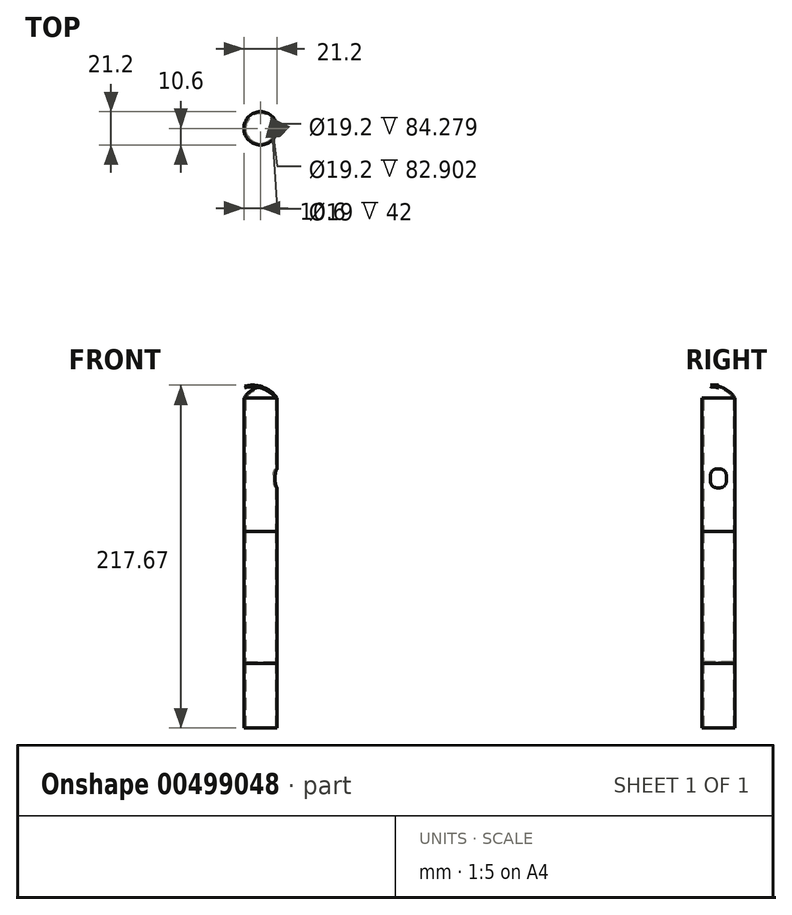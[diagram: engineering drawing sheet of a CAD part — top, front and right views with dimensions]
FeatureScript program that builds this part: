
annotation { "Feature Type Name" : "Feature", "Feature Type Description" : "" }
export const myFeature = defineFeature(function(context is Context, id is Id, definition is map)
    precondition{}
    {
        {
            var Q0;
            Q0=qCreatedBy(makeId("Front.planeOp"),FACE);
            var sketch = newSketch(context, id + "F0", { "sketchPlane" : qUnion([Q0])});
            skLineSegment(sketch, "E0", {"start": v(0, -33) * mm, "end": v(0, 176.5) * mm});
            skLineSegment(sketch, "E1", {"start": v(0, -33) * mm, "end": v(-10.5, -33) * mm});
            skLineSegment(sketch, "E2", {"start": v(-10.5, -33) * mm, "end": v(-10.5, 8) * mm});
            skLineSegment(sketch, "E3", {"start": v(-10.5, 8) * mm, "end": v(-10.6, 8) * mm});
            skLineSegment(sketch, "E4", {"start": v(-10.6, 8) * mm, "end": v(-10.6, 176.5) * mm});
            skArc(sketch, "E5", {"start": v(0, 184) * mm, "mid": v(-5.96, 181.18) * mm, "end": v(-10.6, 176.5) * mm});
            skLineSegment(sketch, "E6", {"start": v(0, 176.5) * mm, "end": v(0, 184) * mm});
            skSolve(sketch);
        }
        {
            var Q0;
            Q0=makeQuery(id+"F0.imprint","IMPRINT",FACE,{"disambiguationData":[TD([[makeQuery(id+"F0.imprint","IMPRINT",EDGE,{"derivedFrom":sQuery(id+"F0.wireOp",EDGE,"E0")}),1.0]])]});
            var Q1;
            Q1=sQuery(id+"F0.wireOp",EDGE,"E6");
            revolve(context, id + "F1", {"entities" : qUnion([Q0]), "axis" : qUnion([Q1]), "revolveType" : RevolveType.FULL});
        }
        {
            var Q0;
            Q0=makeQuery(id+"F1.opRevolve","SWEPT_FACE",FACE,{"disambiguationData":[OSD([sQuery(id+"F0.wireOp",EDGE,"E1")])]});
            shell(context, id + "F2", {"entities" : qUnion([Q0]), "thickness" : 1 * mm});
        }
        {
            var Q0;
            Q0=qCreatedBy(makeId("Right.planeOp"),FACE);
            var sketch = newSketch(context, id + "F3", { "sketchPlane" : qUnion([Q0])});
            skLineSegment(sketch, "E7.bottom", {"start": v(1, 131.5) * mm, "end": v(-1, 131.5) * mm});
            skLineSegment(sketch, "E7.top", {"start": v(1, 119.5) * mm, "end": v(-1, 119.5) * mm});
            skLineSegment(sketch, "E7.left", {"start": v(5, 127.5) * mm, "end": v(5, 123.5) * mm});
            skLineSegment(sketch, "E7.right", {"start": v(-5, 127.5) * mm, "end": v(-5, 123.5) * mm});
            skPoint(sketch, "E7.middle", {"position": v(0, 125.5) * mm});
            skPoint(sketch, "E8.visualSharp", {"position": v(5, 131.5) * mm});
            skArc(sketch, "E8.filletArc", {"start": v(5, 127.5) * mm, "mid": v(3.83, 130.33) * mm, "end": v(1, 131.5) * mm});
            skPoint(sketch, "E9.visualSharp", {"position": v(5, 119.5) * mm});
            skArc(sketch, "E9.filletArc", {"start": v(1, 119.5) * mm, "mid": v(3.83, 120.67) * mm, "end": v(5, 123.5) * mm});
            skPoint(sketch, "E10.visualSharp", {"position": v(-5, 119.5) * mm});
            skArc(sketch, "E10.filletArc", {"start": v(-5, 123.5) * mm, "mid": v(-3.83, 120.67) * mm, "end": v(-1, 119.5) * mm});
            skPoint(sketch, "E11.visualSharp", {"position": v(-5, 131.5) * mm});
            skArc(sketch, "E11.filletArc", {"start": v(-1, 131.5) * mm, "mid": v(-3.83, 130.33) * mm, "end": v(-5, 127.5) * mm});
            skSolve(sketch);
        }
        {
            var Q0;
            Q0 = qSketchRegion(id + "F3", true);
            extrude(context, id + "F4", {"entities" : qUnion([Q0]), "operationType" : NewBodyOperationType.REMOVE, "depth" : 21.9 * mm});
        }
        {
            var Q0;
            Q0=qCreatedBy(makeId("Right.planeOp"),FACE);
            var sketch = newSketch(context, id + "F5", { "sketchPlane" : qUnion([Q0])});
            skLineSegment(sketch, "E12", {"start": v(19.75, 91.9) * mm, "end": v(-25.96, 91.9) * mm});
            skSolve(sketch);
        }
        {
            var Q0;
            Q0=sQuery(id+"F5.wireOp",EDGE,"E12");
            extrude(context, id + "F6", {"bodyType" : ToolBodyType.SURFACE, "surfaceEntities" : qUnion([Q0]), "endBound" : BoundingType.SYMMETRIC, "depth" : 50 * mm});
        }
        {
            var Q0;
            Q0=makeQuery(id+"F6.opExtrude","SWEPT_FACE",FACE,{"disambiguationData":[OSD([sQuery(id+"F5.wireOp",EDGE,"E12")])]});
            extrude(context, id + "F7", {"entities" : qUnion([Q0]), "operationType" : NewBodyOperationType.REMOVE, "oppositeDirection" : true, "depth" : 0.01 * mm});
        }
    });
